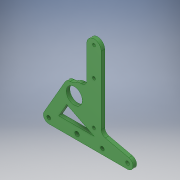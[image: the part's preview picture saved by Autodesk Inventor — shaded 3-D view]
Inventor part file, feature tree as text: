
AUTODESK INVENTOR PART (.ipt)
format: ipt  version: 2017 SP1 (Build 210196100, 196)  size: 169,984 bytes
history: native  units: in
note: dims shown in document units (in); Inventor stores cm internally (conversion verified against a paired STEP export)
features: extrude x1, chamfer x1
ambient origin geometry x8: Origin, YZ Plane, XZ Plane, XY Plane, X Axis, Y Axis, Z Axis, Center Point
bodies: Solid1 (feature_tree)
feature tree (2):
  extrude  "Extrusion1"  Depth=0.21in
  chamfer  "Chamfer1"  Distance=3.0in
